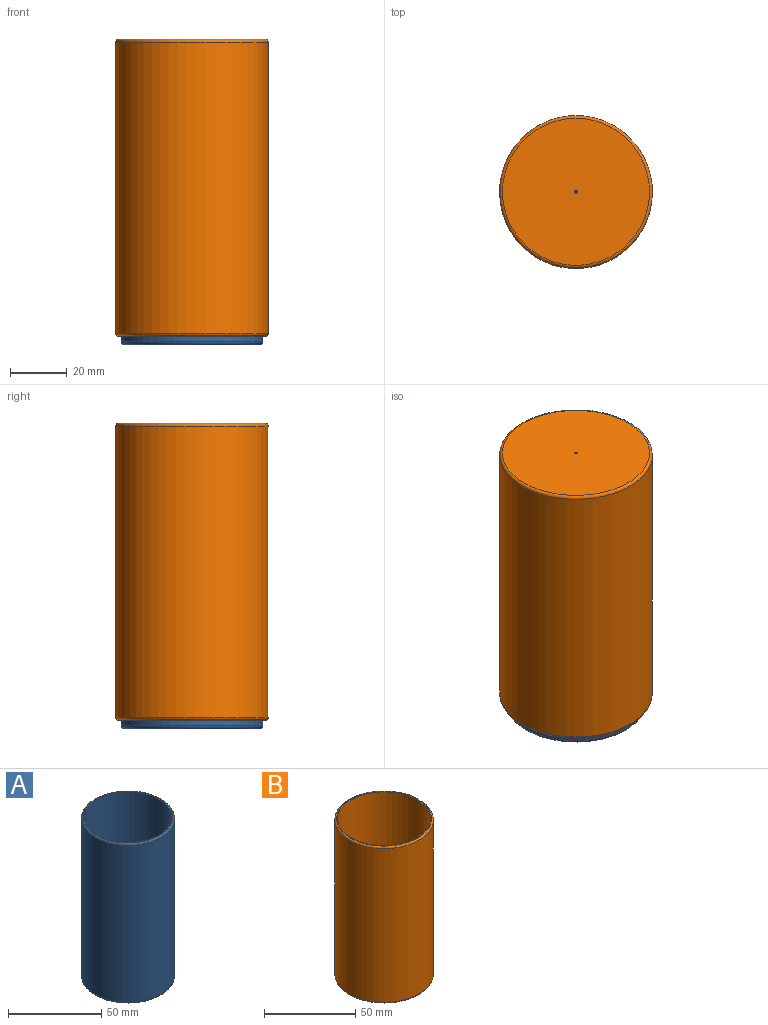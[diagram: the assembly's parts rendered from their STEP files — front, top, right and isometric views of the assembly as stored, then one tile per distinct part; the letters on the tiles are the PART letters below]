
ASSEMBLY  parts=2 mates=1
PART A: 8 faces, bbox 54.1x54.1x105 mm
  f0: cylinder r=23.5mm len=100mm, axis (0,0,-1), area 14765.5mm2, adj f2,f3
  f1: cylinder r=25mm len=103mm, axis (0,0,-1), area 16179.2mm2, adj f5,f6
  f2: plane 48x48mm, normal (0,0,1), area 74.6mm2, adj f0,f6
  f3: plane 47x47mm, normal (0,0,1), area 1734.2mm2, adj f0,f7
  f4: plane 48x48mm, normal (0,0,-1), area 1808.8mm2, adj f5,f7
  f5: torus R=24mm, axis (0,0,1), area 243.2mm2, adj f1,f4
  f6: torus R=24mm, axis (0,0,1), area 243.2mm2, adj f1,f2
  f7: cylinder r=0.5mm len=5mm, axis (0,0,1), area 15.7mm2, adj f3,f4
PART B: 8 faces, bbox 58.4x58.4x105 mm
  f0: cylinder r=25.5mm len=100mm, axis (0,0,-1), area 16022.1mm2, adj f2,f3
  f1: cylinder r=27mm len=103mm, axis (0,0,-1), area 17473.5mm2, adj f5,f6
  f2: plane 52x52mm, normal (0,0,1), area 80.9mm2, adj f0,f6
  f3: plane 51x51mm, normal (0,0,1), area 2042mm2, adj f0,f7
  f4: plane 52x52mm, normal (0,0,-1), area 2122.9mm2, adj f5,f7
  f5: torus R=26mm, axis (0,0,1), area 262.9mm2, adj f1,f4
  f6: torus R=26mm, axis (0,0,1), area 262.9mm2, adj f1,f2
  f7: cylinder r=0.5mm len=5mm, axis (0,0,1), area 15.7mm2, adj f3,f4
PLACE A t=(29.1,-22.13,-50.03)mm
PLACE B rot(axis=(-0.71,-0.71,0),180deg) t=(29.1,-22.13,48.02)mm
MATE slider B.f0 <-> A.f0  axis (0,0,1) through (29.1,-22.13,-50.98)mm
